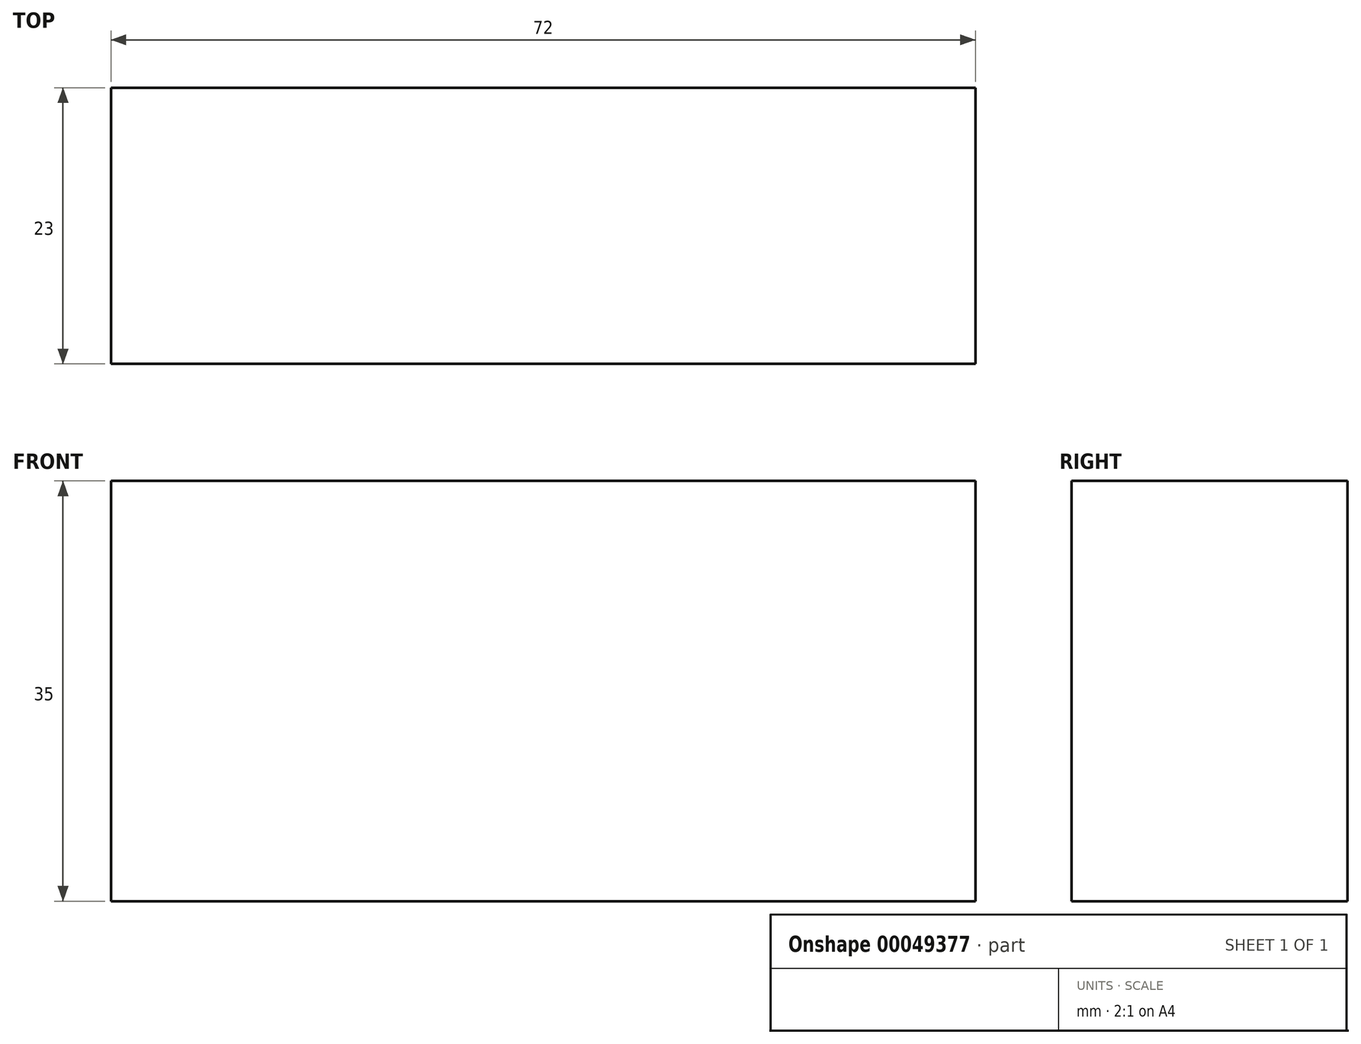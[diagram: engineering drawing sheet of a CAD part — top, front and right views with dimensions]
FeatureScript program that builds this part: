
annotation { "Feature Type Name" : "Feature", "Feature Type Description" : "" }
export const myFeature = defineFeature(function(context is Context, id is Id, definition is map)
    precondition{}
    {
        {
            var Q0;
            Q0=qCreatedBy(makeId("Top.planeOp"),FACE);
            var sketch = newSketch(context, id + "F0", { "sketchPlane" : qUnion([Q0])});
            skLineSegment(sketch, "E0.bottom", {"start": v(0, 0) * mm, "end": v(-72, 0) * mm});
            skLineSegment(sketch, "E0.top", {"start": v(0, -23) * mm, "end": v(-72, -23) * mm});
            skLineSegment(sketch, "E0.left", {"start": v(0, 0) * mm, "end": v(0, -23) * mm});
            skLineSegment(sketch, "E0.right", {"start": v(-72, 0) * mm, "end": v(-72, -23) * mm});
            skSolve(sketch);
        }
        {
            var Q0;
            Q0 = qSketchRegion(id + "F0", true);
            extrude(context, id + "F1", {"entities" : qUnion([Q0]), "depth" : 35 * mm});
        }
    });
